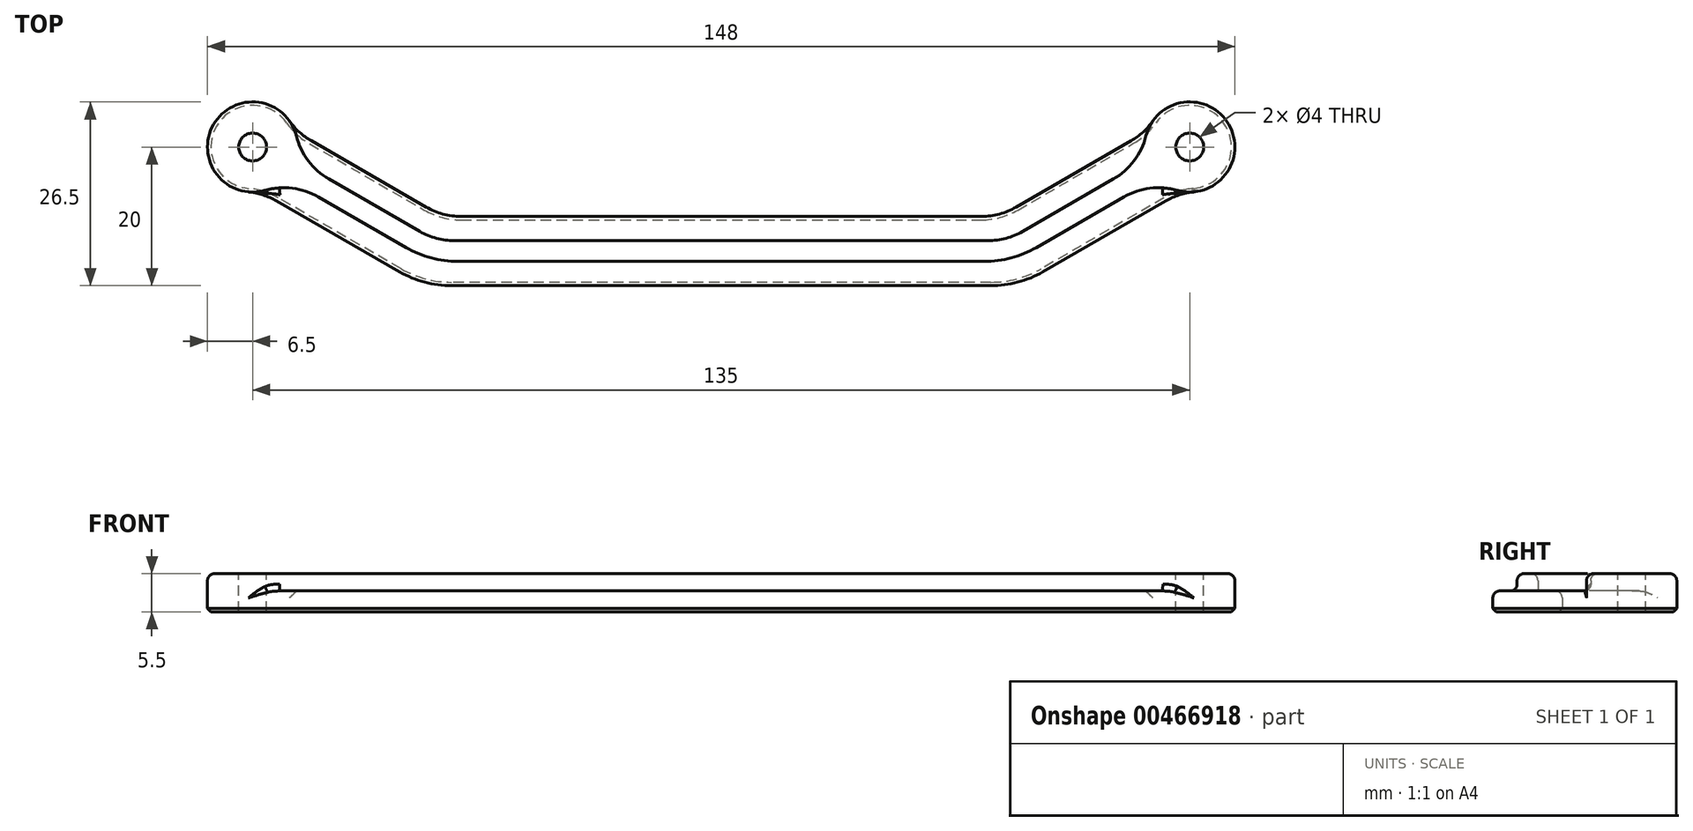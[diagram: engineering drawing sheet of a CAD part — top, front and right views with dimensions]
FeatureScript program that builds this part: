
annotation { "Feature Type Name" : "Feature", "Feature Type Description" : "" }
export const myFeature = defineFeature(function(context is Context, id is Id, definition is map)
    precondition{}
    {
        {
            var Q0;
            Q0=qCreatedBy(makeId("Top.planeOp"),FACE);
            var sketch = newSketch(context, id + "F0", { "sketchPlane" : qUnion([Q0])});
            skLineSegment(sketch, "E0", {"start": v(0, 0) * mm, "end": v(67.5, 0) * mm, "construction": true});
            skLineSegment(sketch, "E1", {"start": v(0, 0) * mm, "end": v(0, 13.51) * mm, "construction": true});
            skCircle(sketch, "E2", {"center": v(67.5, 0) * mm, "radius": 6.5 * mm});
            skCircle(sketch, "E3.MirrorC", {"center": v(-67.5, 0) * mm, "radius": 6.5 * mm});
            skSolve(sketch);
        }
        {
            var Q0;
            Q0=qSketchRegion(id+"F0",true);
            extrude(context, id + "F1", {"entities" : qUnion([Q0]), "depth" : 5.5 * mm, "offsetDistance" : 25 * mm});
        }
        {
            var Q0;
            Q0=qCreatedBy(makeId("Top.planeOp"),FACE);
            var sketch = newSketch(context, id + "F2", { "sketchPlane" : qUnion([Q0])});
            skLineSegment(sketch, "E4", {"start": v(-67.5, 0) * mm, "end": v(67.5, 0) * mm, "construction": true});
            skLineSegment(sketch, "E5", {"start": v(-67.5, 0) * mm, "end": v(-41.52, -15) * mm, "construction": true});
            skLineSegment(sketch, "E6", {"start": v(-41.52, -15) * mm, "end": v(0, -15) * mm, "construction": true});
            skLineSegment(sketch, "E7", {"start": v(0, -15) * mm, "end": v(0, 0) * mm, "construction": true});
            skLineSegment(sketch, "E8.MirrorCS", {"start": v(41.52, -15) * mm, "end": v(0, -15) * mm, "construction": true});
            skLineSegment(sketch, "E9.MirrorCS", {"start": v(67.5, 0) * mm, "end": v(41.52, -15) * mm, "construction": true});
            skLineSegment(sketch, "E10.0", {"start": v(70, -4.33) * mm, "end": v(42.86, -20) * mm});
            skLineSegment(sketch, "E10.1", {"start": v(42.86, -20) * mm, "end": v(0, -20) * mm});
            skLineSegment(sketch, "E10.2", {"start": v(-42.86, -20) * mm, "end": v(0, -20) * mm});
            skLineSegment(sketch, "E10.3", {"start": v(-70, -4.33) * mm, "end": v(-42.86, -20) * mm});
            skLineSegment(sketch, "E11.0", {"start": v(65, 4.33) * mm, "end": v(40.18, -10) * mm});
            skLineSegment(sketch, "E11.1", {"start": v(40.18, -10) * mm, "end": v(0, -10) * mm});
            skLineSegment(sketch, "E11.2", {"start": v(-40.18, -10) * mm, "end": v(0, -10) * mm});
            skLineSegment(sketch, "E11.3", {"start": v(-65, 4.33) * mm, "end": v(-40.18, -10) * mm});
            skLineSegment(sketch, "E12", {"start": v(-70, -4.33) * mm, "end": v(-65, 4.33) * mm});
            skLineSegment(sketch, "E13", {"start": v(65, 4.33) * mm, "end": v(70, -4.33) * mm});
            skSolve(sketch);
        }
        {
            var Q0;
            Q0=qSketchRegion(id+"F2",true);
            extrude(context, id + "F3", {"entities" : qUnion([Q0]), "operationType" : NewBodyOperationType.ADD, "depth" : 3 * mm, "offsetDistance" : 25 * mm});
        }
        {
            var Q0;
            Q0=makeQuery(id+"F3.opExtrude","CAP_FACE",FACE,{"disambiguationData":[OSD([sQuery(id+"F2.wireOp",EDGE,"E10.0"),sQuery(id+"F2.wireOp",EDGE,"E10.1"),sQuery(id+"F2.wireOp",EDGE,"E10.2"),sQuery(id+"F2.wireOp",EDGE,"E10.3"),sQuery(id+"F2.wireOp",EDGE,"E11.0"),sQuery(id+"F2.wireOp",EDGE,"E11.1"),sQuery(id+"F2.wireOp",EDGE,"E11.2"),sQuery(id+"F2.wireOp",EDGE,"E11.3"),sQuery(id+"F2.wireOp",EDGE,"E12"),sQuery(id+"F2.wireOp",EDGE,"E13")])],"isStart":false});
            var sketch = newSketch(context, id + "F4", { "sketchPlane" : qUnion([Q0])});
            skLineSegment(sketch, "E14.0", {"start": v(68.25, -1.3) * mm, "end": v(41.92, -16.5) * mm});
            skLineSegment(sketch, "E14.1", {"start": v(41.92, -16.5) * mm, "end": v(0, -16.5) * mm});
            skLineSegment(sketch, "E14.2", {"start": v(-41.92, -16.5) * mm, "end": v(0, -16.5) * mm});
            skLineSegment(sketch, "E14.3", {"start": v(-68.25, -1.3) * mm, "end": v(-41.92, -16.5) * mm});
            skLineSegment(sketch, "E15.0", {"start": v(66.75, 1.3) * mm, "end": v(41.12, -13.5) * mm});
            skLineSegment(sketch, "E15.1", {"start": v(41.12, -13.5) * mm, "end": v(0, -13.5) * mm});
            skLineSegment(sketch, "E15.2", {"start": v(-41.12, -13.5) * mm, "end": v(0, -13.5) * mm});
            skLineSegment(sketch, "E15.3", {"start": v(-66.75, 1.3) * mm, "end": v(-41.12, -13.5) * mm});
            skLineSegment(sketch, "E16", {"start": v(-68.25, -1.3) * mm, "end": v(-66.75, 1.3) * mm});
            skLineSegment(sketch, "E17", {"start": v(66.75, 1.3) * mm, "end": v(68.25, -1.3) * mm});
            skSolve(sketch);
        }
        {
            var Q0;
            Q0=qSketchRegion(id+"F4",true);
            var Q1;
            Q1=makeQuery(id+"F1.opExtrude","CAP_FACE",FACE,{"disambiguationData":[OSD([sQuery(id+"F0.wireOp",EDGE,"E3.MirrorC")])],"isStart":false});
            extrude(context, id + "F5", {"entities" : qUnion([Q0]), "operationType" : NewBodyOperationType.ADD, "endBound" : BoundingType.UP_TO_SURFACE, "endBoundEntityFace" : qUnion([Q1]), "depth" : 25 * mm, "offsetDistance" : 25 * mm});
        }
        {
            var Q0;
            Q0=makeQuery(id+"F5.boolean.opBoolean","MERGE",FACE,{"derivedFrom":[makeQuery(id+"F1.opExtrude","CAP_FACE",FACE,{"disambiguationData":[OSD([sQuery(id+"F0.wireOp",EDGE,"E2")])],"isStart":false}),makeQuery(id+"F1.opExtrude","CAP_FACE",FACE,{"disambiguationData":[OSD([sQuery(id+"F0.wireOp",EDGE,"E3.MirrorC")])],"isStart":false}),makeQuery(id+"F5.opExtrude","CAP_FACE",FACE,{"disambiguationData":[OSD([sQuery(id+"F4.wireOp",EDGE,"E14.0"),sQuery(id+"F4.wireOp",EDGE,"E14.1"),sQuery(id+"F4.wireOp",EDGE,"E14.2"),sQuery(id+"F4.wireOp",EDGE,"E14.3"),sQuery(id+"F4.wireOp",EDGE,"E15.0"),sQuery(id+"F4.wireOp",EDGE,"E15.1"),sQuery(id+"F4.wireOp",EDGE,"E15.2"),sQuery(id+"F4.wireOp",EDGE,"E15.3"),sQuery(id+"F4.wireOp",EDGE,"E16"),sQuery(id+"F4.wireOp",EDGE,"E17")])],"isStart":false})]});
            var sketch = newSketch(context, id + "F6", { "sketchPlane" : qUnion([Q0])});
            skCircle(sketch, "E18", {"center": v(-67.5, 0) * mm, "radius": 2 * mm});
            skCircle(sketch, "E19", {"center": v(67.5, 0) * mm, "radius": 2 * mm});
            skSolve(sketch);
        }
        {
            var Q0;
            Q0=qSketchRegion(id+"F6",true);
            extrude(context, id + "F7", {"entities" : qUnion([Q0]), "operationType" : NewBodyOperationType.REMOVE, "endBound" : BoundingType.THROUGH_ALL, "oppositeDirection" : true, "depth" : 25 * mm, "offsetDistance" : 25 * mm});
        }
        {
            var Q0;
            Q0=makeQuery(id+"F3.boolean.opBoolean","INTERSECT",EDGE,{"derivedFrom":[makeQuery(id+"F1.opExtrude","SWEPT_FACE",FACE,{"disambiguationData":[OSD([sQuery(id+"F0.wireOp",EDGE,"E3.MirrorC")])]}),makeQuery(id+"F3.opExtrude","SWEPT_FACE",FACE,{"disambiguationData":[OSD([sQuery(id+"F2.wireOp",EDGE,"E10.3")])]})]});
            var Q1;
            Q1=makeQuery(id+"F3.boolean.opBoolean","INTERSECT",EDGE,{"derivedFrom":[makeQuery(id+"F1.opExtrude","SWEPT_FACE",FACE,{"disambiguationData":[OSD([sQuery(id+"F0.wireOp",EDGE,"E2")])]}),makeQuery(id+"F3.opExtrude","SWEPT_FACE",FACE,{"disambiguationData":[OSD([sQuery(id+"F2.wireOp",EDGE,"E10.0")])]})]});
            var Q2;
            Q2=makeQuery(id+"F3.boolean.opBoolean","INTERSECT",EDGE,{"derivedFrom":[makeQuery(id+"F1.opExtrude","SWEPT_FACE",FACE,{"disambiguationData":[OSD([sQuery(id+"F0.wireOp",EDGE,"E3.MirrorC")])]}),makeQuery(id+"F3.opExtrude","SWEPT_FACE",FACE,{"disambiguationData":[OSD([sQuery(id+"F2.wireOp",EDGE,"E11.3")])]})]});
            var Q3;
            Q3=makeQuery(id+"F3.boolean.opBoolean","INTERSECT",EDGE,{"derivedFrom":[makeQuery(id+"F1.opExtrude","SWEPT_FACE",FACE,{"disambiguationData":[OSD([sQuery(id+"F0.wireOp",EDGE,"E2")])]}),makeQuery(id+"F3.opExtrude","SWEPT_FACE",FACE,{"disambiguationData":[OSD([sQuery(id+"F2.wireOp",EDGE,"E11.0")])]})]});
            fillet(context, id + "F8", {"entities" : qUnion([Q0, Q1, Q2, Q3]), "radius" : 10 * mm, "tangentPropagation" : true, "allowEdgeOverflow" : false});
        }
        {
            var Q0;
            Q0=makeQuery(id+"F5.boolean.opBoolean","INTERSECT",EDGE,{"derivedFrom":[makeQuery(id+"F1.opExtrude","SWEPT_FACE",FACE,{"disambiguationData":[OSD([sQuery(id+"F0.wireOp",EDGE,"E2")])]}),makeQuery(id+"F5.opExtrude","SWEPT_FACE",FACE,{"disambiguationData":[OSD([sQuery(id+"F4.wireOp",EDGE,"E15.0")])]})]});
            var Q1;
            Q1=makeQuery(id+"F3.opExtrude","SWEPT_EDGE",EDGE,{"disambiguationData":[OSD([sQuery(id+"F2.wireOp",EDGE,"E11.0"),sQuery(id+"F2.wireOp",EDGE,"E11.1")])]});
            var Q2;
            Q2=makeQuery(id+"F5.opExtrude","SWEPT_EDGE",EDGE,{"disambiguationData":[OSD([sQuery(id+"F4.wireOp",EDGE,"E15.0"),sQuery(id+"F4.wireOp",EDGE,"E15.1")])]});
            var Q3;
            Q3=makeQuery(id+"F5.opExtrude","SWEPT_EDGE",EDGE,{"disambiguationData":[OSD([sQuery(id+"F4.wireOp",EDGE,"E15.2"),sQuery(id+"F4.wireOp",EDGE,"E15.3")])]});
            var Q4;
            Q4=makeQuery(id+"F3.opExtrude","SWEPT_EDGE",EDGE,{"disambiguationData":[OSD([sQuery(id+"F2.wireOp",EDGE,"E11.2"),sQuery(id+"F2.wireOp",EDGE,"E11.3")])]});
            var Q5;
            Q5=makeQuery(id+"F5.boolean.opBoolean","INTERSECT",EDGE,{"derivedFrom":[makeQuery(id+"F1.opExtrude","SWEPT_FACE",FACE,{"disambiguationData":[OSD([sQuery(id+"F0.wireOp",EDGE,"E3.MirrorC")])]}),makeQuery(id+"F5.opExtrude","SWEPT_FACE",FACE,{"disambiguationData":[OSD([sQuery(id+"F4.wireOp",EDGE,"E15.3")])]})]});
            var Q6;
            Q6=makeQuery(id+"F5.boolean.opBoolean","INTERSECT",EDGE,{"derivedFrom":[makeQuery(id+"F1.opExtrude","SWEPT_FACE",FACE,{"disambiguationData":[OSD([sQuery(id+"F0.wireOp",EDGE,"E3.MirrorC")])]}),makeQuery(id+"F5.opExtrude","SWEPT_FACE",FACE,{"disambiguationData":[OSD([sQuery(id+"F4.wireOp",EDGE,"E14.3")])]})]});
            var Q7;
            Q7=makeQuery(id+"F5.boolean.opBoolean","INTERSECT",EDGE,{"derivedFrom":[makeQuery(id+"F1.opExtrude","SWEPT_FACE",FACE,{"disambiguationData":[OSD([sQuery(id+"F0.wireOp",EDGE,"E2")])]}),makeQuery(id+"F5.opExtrude","SWEPT_FACE",FACE,{"disambiguationData":[OSD([sQuery(id+"F4.wireOp",EDGE,"E14.0")])]})]});
            fillet(context, id + "F9", {"entities" : qUnion([Q0, Q1, Q2, Q3, Q4, Q5, Q6, Q7]), "radius" : 10 * mm, "tangentPropagation" : true, "allowEdgeOverflow" : false});
        }
        {
            var Q0;
            Q0=makeQuery(id+"F3.opExtrude","SWEPT_EDGE",EDGE,{"disambiguationData":[OSD([sQuery(id+"F2.wireOp",EDGE,"E10.0"),sQuery(id+"F2.wireOp",EDGE,"E10.1")])]});
            var Q1;
            Q1=makeQuery(id+"F5.opExtrude","SWEPT_EDGE",EDGE,{"disambiguationData":[OSD([sQuery(id+"F4.wireOp",EDGE,"E14.0"),sQuery(id+"F4.wireOp",EDGE,"E14.1")])]});
            var Q2;
            Q2=makeQuery(id+"F3.opExtrude","SWEPT_EDGE",EDGE,{"disambiguationData":[OSD([sQuery(id+"F2.wireOp",EDGE,"E10.2"),sQuery(id+"F2.wireOp",EDGE,"E10.3")])]});
            var Q3;
            Q3=makeQuery(id+"F5.opExtrude","SWEPT_EDGE",EDGE,{"disambiguationData":[OSD([sQuery(id+"F4.wireOp",EDGE,"E14.2"),sQuery(id+"F4.wireOp",EDGE,"E14.3")])]});
            fillet(context, id + "F10", {"entities" : qUnion([Q0, Q1, Q2, Q3]), "radius" : 15 * mm, "tangentPropagation" : true, "allowEdgeOverflow" : false});
        }
        {
            var Q0;
            Q0=makeQuery(id+"F3.opExtrude","CAP_EDGE",EDGE,{"disambiguationData":[OSD([sQuery(id+"F2.wireOp",EDGE,"E10.1"),sQuery(id+"F2.wireOp",EDGE,"E10.2")])],"isStart":false});
            var Q1;
            {var subQ0=sQuery(id+"F4.wireOp",EDGE,"E14.3");var subQ1=sQuery(id+"F4.wireOp",EDGE,"E14.2");Q1=makeQuery(id+"F10.opFillet","BLEND_EDGE",EDGE,{"blendedFrom":[makeQuery(id+"F5.opExtrude","SWEPT_EDGE",EDGE,{"disambiguationData":[OSD([subQ1,subQ0])]}),makeQuery(id+"F5.boolean.opBoolean","MERGE",FACE,{"derivedFrom":[makeQuery(id+"F1.opExtrude","CAP_FACE",FACE,{"disambiguationData":[OSD([sQuery(id+"F0.wireOp",EDGE,"E2")])],"isStart":false}),makeQuery(id+"F1.opExtrude","CAP_FACE",FACE,{"disambiguationData":[OSD([sQuery(id+"F0.wireOp",EDGE,"E3.MirrorC")])],"isStart":false}),makeQuery(id+"F5.opExtrude","CAP_FACE",FACE,{"disambiguationData":[OSD([sQuery(id+"F4.wireOp",EDGE,"E14.0"),sQuery(id+"F4.wireOp",EDGE,"E14.1"),subQ1,subQ0,sQuery(id+"F4.wireOp",EDGE,"E15.0"),sQuery(id+"F4.wireOp",EDGE,"E15.1"),sQuery(id+"F4.wireOp",EDGE,"E15.2"),sQuery(id+"F4.wireOp",EDGE,"E15.3"),sQuery(id+"F4.wireOp",EDGE,"E16"),sQuery(id+"F4.wireOp",EDGE,"E17")])],"isStart":false})]})],"blendedInto":[makeQuery(id+"F5.boolean.opBoolean","MERGE",FACE,{"derivedFrom":[makeQuery(id+"F1.opExtrude","CAP_FACE",FACE,{"disambiguationData":[OSD([sQuery(id+"F0.wireOp",EDGE,"E2")])],"isStart":false}),makeQuery(id+"F1.opExtrude","CAP_FACE",FACE,{"disambiguationData":[OSD([sQuery(id+"F0.wireOp",EDGE,"E3.MirrorC")])],"isStart":false}),makeQuery(id+"F5.opExtrude","CAP_FACE",FACE,{"disambiguationData":[OSD([sQuery(id+"F4.wireOp",EDGE,"E14.0"),sQuery(id+"F4.wireOp",EDGE,"E14.1"),subQ1,subQ0,sQuery(id+"F4.wireOp",EDGE,"E15.0"),sQuery(id+"F4.wireOp",EDGE,"E15.1"),sQuery(id+"F4.wireOp",EDGE,"E15.2"),sQuery(id+"F4.wireOp",EDGE,"E15.3"),sQuery(id+"F4.wireOp",EDGE,"E16"),sQuery(id+"F4.wireOp",EDGE,"E17")])],"isStart":false})]})]});}
            var Q2;
            Q2=makeQuery(id+"F3.opExtrude","CAP_EDGE",EDGE,{"disambiguationData":[OSD([sQuery(id+"F2.wireOp",EDGE,"E11.3")])],"isStart":false});
            fillet(context, id + "F11", {"entities" : qUnion([Q0, Q1, Q2]), "radius" : 1 * mm, "tangentPropagation" : true, "allowEdgeOverflow" : false});
        }
        {
            var Q0;
            Q0=makeQuery(id+"F3.opExtrude","CAP_EDGE",EDGE,{"disambiguationData":[OSD([sQuery(id+"F2.wireOp",EDGE,"E11.1"),sQuery(id+"F2.wireOp",EDGE,"E11.2")])],"isStart":true});
            chamfer(context, id + "F12", {"entities" : qUnion([Q0]), "width" : .5 * mm, "tangentPropagation" : true});
        }
        {
            var Q0;
            Q0=makeQuery(id+"F5.opExtrude","CAP_EDGE",EDGE,{"disambiguationData":[OSD([sQuery(id+"F4.wireOp",EDGE,"E15.1"),sQuery(id+"F4.wireOp",EDGE,"E15.2")])],"isStart":true});
            var Q1;
            Q1=makeQuery(id+"F5.opExtrude","CAP_EDGE",EDGE,{"disambiguationData":[OSD([sQuery(id+"F4.wireOp",EDGE,"E14.1"),sQuery(id+"F4.wireOp",EDGE,"E14.2")])],"isStart":true});
            fillet(context, id + "F13", {"entities" : qUnion([Q0, Q1]), "radius" : 1 * mm, "tangentPropagation" : true, "allowEdgeOverflow" : false});
        }
    });
